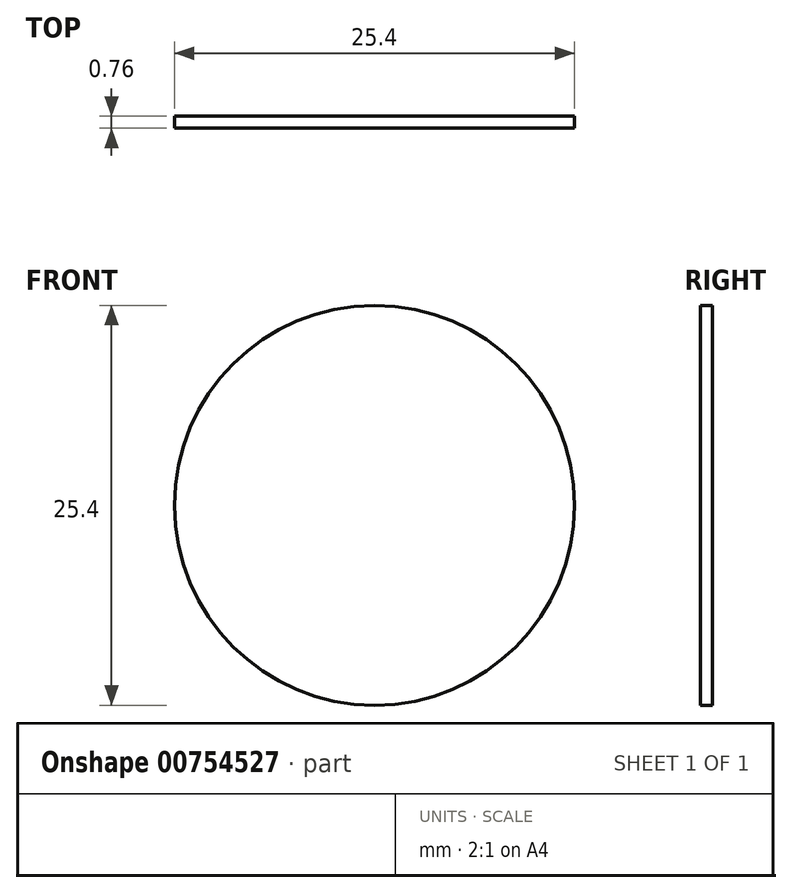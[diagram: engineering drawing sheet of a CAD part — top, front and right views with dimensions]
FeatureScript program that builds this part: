
annotation { "Feature Type Name" : "Feature", "Feature Type Description" : "" }
export const myFeature = defineFeature(function(context is Context, id is Id, definition is map)
    precondition{}
    {
        {
            var Q0;
            Q0=qCreatedBy(makeId("Front.planeOp"),FACE);
            var sketch = newSketch(context, id + "F0", { "sketchPlane" : qUnion([Q0])});
            skCircle(sketch, "E0", {"center": v(0, 0) * mm, "radius": 12.7 * mm});
            skSolve(sketch);
        }
        {
            var Q0;
            Q0 = qSketchRegion(id + "F0", true);
            extrude(context, id + "F1", {"entities" : qUnion([Q0]), "depth" : 0.76 * mm, "offsetDistance" : 25.4 * mm});
        }
    });
